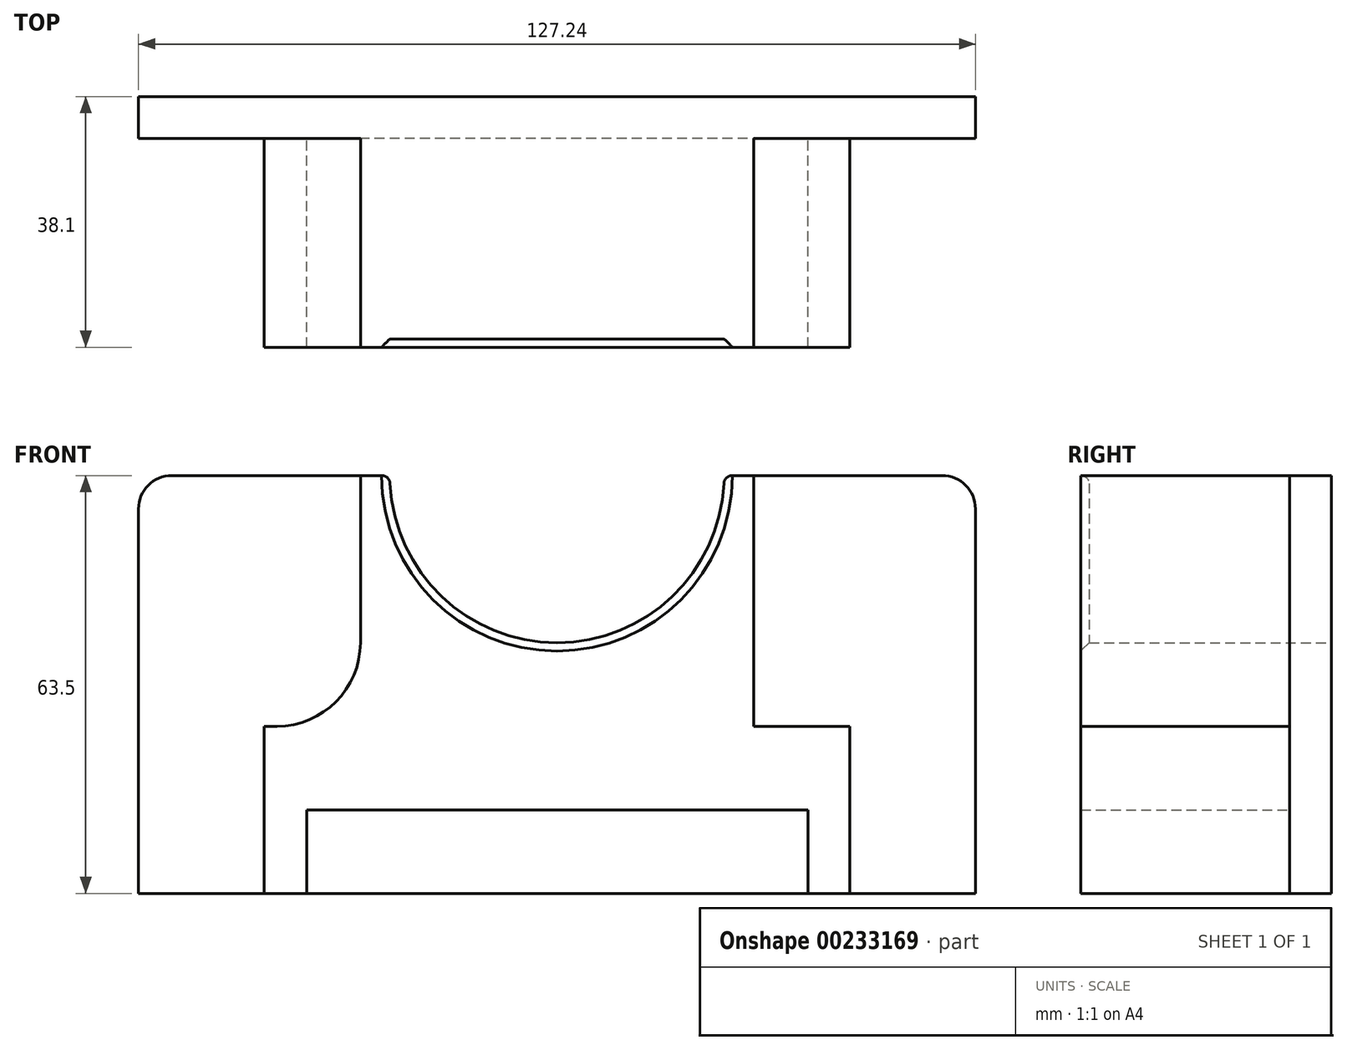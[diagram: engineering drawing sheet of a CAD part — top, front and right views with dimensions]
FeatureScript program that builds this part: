
annotation { "Feature Type Name" : "Feature", "Feature Type Description" : "" }
export const myFeature = defineFeature(function(context is Context, id is Id, definition is map)
    precondition{}
    {
        {
            var Q0;
            Q0=qCreatedBy(makeId("Front.planeOp"),FACE);
            var sketch = newSketch(context, id + "F0", { "sketchPlane" : qUnion([Q0])});
            skLineSegment(sketch, "E0.bottom", {"start": v(63.62, 31.75) * mm, "end": v(25.4, 31.75) * mm});
            skLineSegment(sketch, "E0.top", {"start": v(63.62, -31.75) * mm, "end": v(-63.62, -31.75) * mm});
            skLineSegment(sketch, "E0.left", {"start": v(63.62, 31.75) * mm, "end": v(63.62, -31.75) * mm});
            skLineSegment(sketch, "E0.right", {"start": v(-63.62, 31.75) * mm, "end": v(-63.62, -31.75) * mm});
            skPoint(sketch, "E0.middle", {"position": v(0, 0) * mm});
            skArc(sketch, "E1", {"start": v(-25.4, 31.75) * mm, "mid": v(0, 6.35) * mm, "end": v(25.4, 31.75) * mm});
            skLineSegment(sketch, "E2.trimOffspring", {"start": v(-25.4, 31.75) * mm, "end": v(-63.62, 31.75) * mm});
            skLineSegment(sketch, "E3.top", {"start": v(-29.88, 31.75) * mm, "end": v(-25.4, 31.75) * mm});
            skLineSegment(sketch, "E3.left", {"start": v(-29.88, -6.35) * mm, "end": v(-29.88, 31.75) * mm});
            skLineSegment(sketch, "E3.right", {"start": v(29.88, -6.35) * mm, "end": v(29.88, 31.75) * mm});
            skLineSegment(sketch, "E4.trimOffspring", {"start": v(25.4, 31.75) * mm, "end": v(29.88, 31.75) * mm});
            skLineSegment(sketch, "E5.bottom", {"start": v(-38.03, -19.05) * mm, "end": v(38.17, -19.05) * mm});
            skLineSegment(sketch, "E5.top", {"start": v(-44.52, -6.35) * mm, "end": v(-29.88, -6.35) * mm});
            skLineSegment(sketch, "E5.left", {"start": v(-44.52, -19.05) * mm, "end": v(-44.52, -6.35) * mm});
            skLineSegment(sketch, "E5.right", {"start": v(44.52, -19.05) * mm, "end": v(44.52, -6.35) * mm});
            skPoint(sketch, "E5.middle", {"position": v(0, -12.7) * mm});
            skPoint(sketch, "E6.orphan", {"position": v(-29.88, -12.7) * mm});
            skPoint(sketch, "E7.orphan", {"position": v(29.88, -12.7) * mm});
            skLineSegment(sketch, "E8.trimOffspring", {"start": v(29.88, -6.35) * mm, "end": v(44.52, -6.35) * mm});
            skLineSegment(sketch, "E9.bottom", {"start": v(-44.52, -6.35) * mm, "end": v(-38.03, -6.35) * mm});
            skLineSegment(sketch, "E9.top", {"start": v(-44.52, -31.75) * mm, "end": v(-38.03, -31.75) * mm});
            skLineSegment(sketch, "E9.left", {"start": v(-44.52, -6.35) * mm, "end": v(-44.52, -31.75) * mm});
            skLineSegment(sketch, "E9.right", {"start": v(-38.03, -19.05) * mm, "end": v(-38.03, -31.75) * mm});
            skLineSegment(sketch, "E10.bottom", {"start": v(44.52, -6.35) * mm, "end": v(38.17, -6.35) * mm});
            skLineSegment(sketch, "E10.top", {"start": v(44.52, -31.75) * mm, "end": v(38.17, -31.75) * mm});
            skLineSegment(sketch, "E10.left", {"start": v(44.52, -6.35) * mm, "end": v(44.52, -31.75) * mm});
            skLineSegment(sketch, "E10.right", {"start": v(38.17, -19.05) * mm, "end": v(38.17, -31.75) * mm});
            skSolve(sketch);
        }
        {
            var Q0;
            {var subQ4=sQuery(id+"F0.wireOp",EDGE,"E0.right");Q0=makeQuery(id+"F0.imprint","IMPRINT",FACE,{"disambiguationData":[TD([[makeQuery(id+"F0.imprint","IMPRINT",EDGE,{"derivedFrom":subQ4}),1.0]])]});}
            var Q1;
            Q1=makeQuery(id+"F0.imprint","IMPRINT",FACE,{"disambiguationData":[TD([[makeQuery(id+"F0.imprint","IMPRINT",EDGE,{"derivedFrom":sQuery(id+"F0.wireOp",EDGE,"E0.bottom")}),1.0]])]});
            var Q2;
            Q2=makeQuery(id+"F0.imprint","IMPRINT",FACE,{"disambiguationData":[TD([[makeQuery(id+"F0.imprint","IMPRINT",EDGE,{"derivedFrom":sQuery(id+"F0.wireOp",EDGE,"E1")}),-1.0]])]});
            var Q3;
            Q3=makeQuery(id+"F0.imprint","IMPRINT",FACE,{"disambiguationData":[TD([[makeQuery(id+"F0.imprint","IMPRINT",EDGE,{"derivedFrom":sQuery(id+"F0.wireOp",EDGE,"E5.bottom")}),-1.0]])]});
            extrude(context, id + "F1", {"entities" : qUnion([Q0, Q1, Q2, Q3]), "depth" : 6.35 * mm});
        }
        {
            var Q0;
            Q0=makeQuery(id+"F0.imprint","IMPRINT",FACE,{"disambiguationData":[TD([[makeQuery(id+"F0.imprint","IMPRINT",EDGE,{"derivedFrom":sQuery(id+"F0.wireOp",EDGE,"E1")}),-1.0]])]});
            extrude(context, id + "F2", {"entities" : qUnion([Q0]), "operationType" : NewBodyOperationType.ADD, "depth" : 38.1 * mm});
        }
        {
            var Q0;
            Q0=makeQuery(id+"F1.opExtrude","SWEPT_EDGE",EDGE,{"disambiguationData":[OSD([sQuery(id+"F0.wireOp",EDGE,"E0.right"),sQuery(id+"F0.wireOp",EDGE,"E2.trimOffspring")])]});
            var Q1;
            Q1=makeQuery(id+"F1.opExtrude","SWEPT_EDGE",EDGE,{"disambiguationData":[OSD([sQuery(id+"F0.wireOp",EDGE,"E0.bottom"),sQuery(id+"F0.wireOp",EDGE,"E0.left")])]});
            fillet(context, id + "F3", {"entities" : qUnion([Q0, Q1]), "radius" : 5.08 * mm, "tangentPropagation" : true, "allowEdgeOverflow" : false});
        }
        {
            var Q0;
            Q0=makeQuery(id+"F2.opExtrude","CAP_EDGE",EDGE,{"disambiguationData":[OSD([sQuery(id+"F0.wireOp",EDGE,"E1")])],"isStart":false});
            chamfer(context, id + "F4", {"entities" : qUnion([Q0]), "width" : 1.27 * mm, "tangentPropagation" : true});
        }
        {
            var Q0;
            {var subQ0=sQuery(id+"F0.wireOp",EDGE,"E4.trimOffspring");var subQ1=sQuery(id+"F0.wireOp",EDGE,"E1");Q0=makeQuery(id+"F2.boolean.opBoolean","MERGE",EDGE,{"derivedFrom":[makeQuery(id+"F1.opExtrude","SWEPT_EDGE",EDGE,{"disambiguationData":[OSD([subQ1,subQ0])]}),makeQuery(id+"F2.opExtrude","SWEPT_EDGE",EDGE,{"disambiguationData":[OSD([subQ1,subQ0])]})]});}
            var Q1;
            {var subQ0=sQuery(id+"F0.wireOp",EDGE,"E3.top");var subQ1=sQuery(id+"F0.wireOp",EDGE,"E1");Q1=makeQuery(id+"F2.boolean.opBoolean","MERGE",EDGE,{"derivedFrom":[makeQuery(id+"F1.opExtrude","SWEPT_EDGE",EDGE,{"disambiguationData":[OSD([subQ1,subQ0])]}),makeQuery(id+"F2.opExtrude","SWEPT_EDGE",EDGE,{"disambiguationData":[OSD([subQ1,subQ0])]})]});}
            fillet(context, id + "F5", {"entities" : qUnion([Q0, Q1]), "radius" : 1.27 * mm, "tangentPropagation" : true, "allowEdgeOverflow" : false});
        }
        {
            var Q0;
            Q0=makeQuery(id+"F2.opExtrude","SWEPT_EDGE",EDGE,{"disambiguationData":[OSD([sQuery(id+"F0.wireOp",EDGE,"E3.left"),sQuery(id+"F0.wireOp",EDGE,"E5.top")])]});
            fillet(context, id + "F6", {"entities" : qUnion([Q0]), "radius" : 12.7 * mm, "tangentPropagation" : true, "allowEdgeOverflow" : false});
        }
    });
